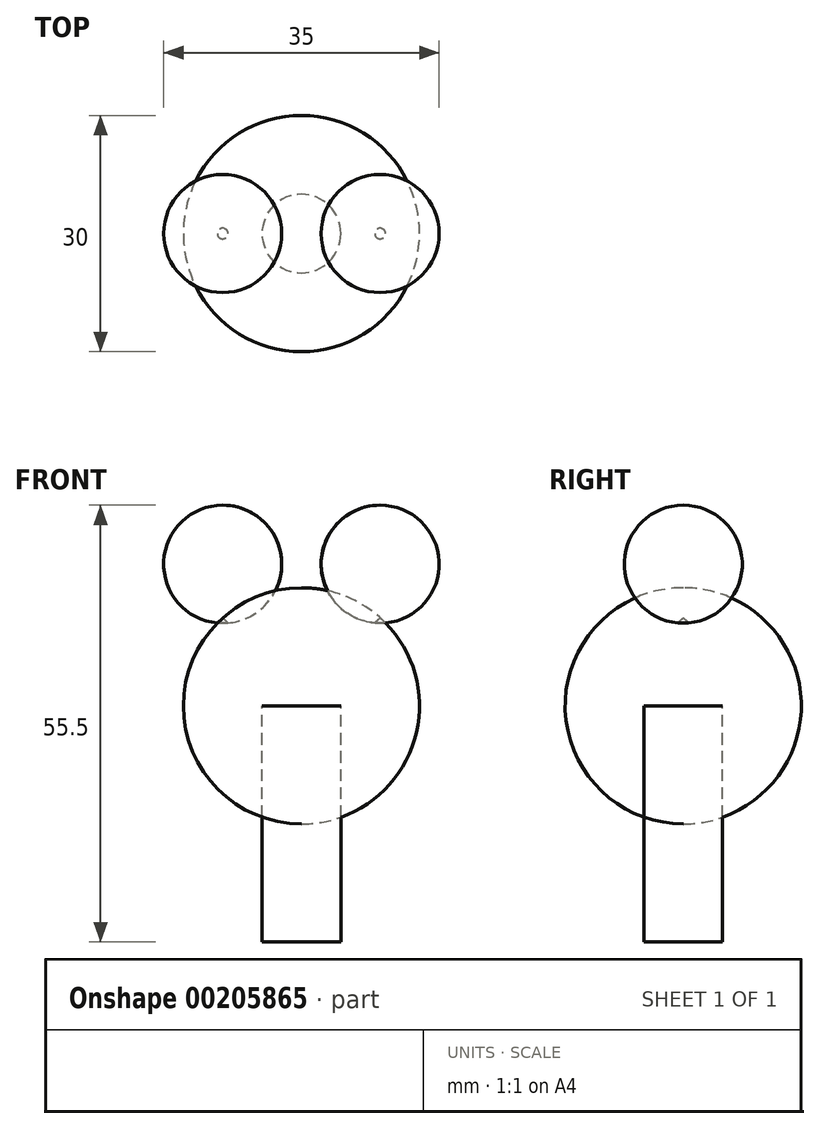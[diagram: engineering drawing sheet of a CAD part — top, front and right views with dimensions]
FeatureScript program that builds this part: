
annotation { "Feature Type Name" : "Feature", "Feature Type Description" : "" }
export const myFeature = defineFeature(function(context is Context, id is Id, definition is map)
    precondition{}
    {
        {
            var Q0;
            Q0=qCreatedBy(makeId("Front.planeOp"),FACE);
            var sketch = newSketch(context, id + "F0", { "sketchPlane" : qUnion([Q0])});
            skArc(sketch, "E0", {"start": v(0, 15) * mm, "mid": v(-15, 0) * mm, "end": v(0, -15) * mm});
            skArc(sketch, "E1", {"start": v(-10, 25.5) * mm, "mid": v(-17.5, 18) * mm, "end": v(-10, 10.5) * mm});
            skLineSegment(sketch, "E2", {"start": v(0, 49.4) * mm, "end": v(0, -36.14) * mm, "construction": true});
            skLineSegment(sketch, "E3", {"start": v(-10, 18) * mm, "end": v(-10, 43.94) * mm, "construction": true});
            skLineSegment(sketch, "E4", {"start": v(0, 15) * mm, "end": v(0, -15) * mm});
            skLineSegment(sketch, "E5", {"start": v(-10, 25.5) * mm, "end": v(-10, 10.5) * mm});
            skSolve(sketch);
        }
        {
            var Q0;
            {var subQ0=sQuery(id+"F0.wireOp",EDGE,"E4");Q0=makeQuery(id+"F0.imprint","IMPRINT",FACE,{"disambiguationData":[TD([[makeQuery(id+"F0.imprint","IMPRINT",EDGE,{"derivedFrom":subQ0}),-1.0]])]});}
            var Q1;
            {var subQ0=sQuery(id+"F0.wireOp",EDGE,"E5");var subQ1=sQuery(id+"F0.wireOp",EDGE,"E0");var subQ2=makeQuery(id+"F0.imprint","INTERSECT",VERTEX,{"derivedFrom":[subQ1,subQ0]});Q1=makeQuery(id+"F0.imprint","IMPRINT",FACE,{"disambiguationData":[TD([[makeQuery(id+"F0.imprint","IMPRINT",EDGE,{"disambiguationData":[TD([[subQ2,-1.0]])],"derivedFrom":subQ1}),1.0]])]});}
            var Q2;
            Q2=sQuery(id+"F0.wireOp",EDGE,"E2");
            revolve(context, id + "F1", {"entities" : qUnion([Q0, Q1]), "axis" : qUnion([Q2]), "revolveType" : RevolveType.FULL});
        }
        {
            var Q0;
            {var subQ0=sQuery(id+"F0.wireOp",EDGE,"E5");var subQ1=sQuery(id+"F0.wireOp",EDGE,"E0");var subQ2=makeQuery(id+"F0.imprint","INTERSECT",VERTEX,{"derivedFrom":[subQ1,subQ0]});Q0=makeQuery(id+"F0.imprint","IMPRINT",FACE,{"disambiguationData":[TD([[makeQuery(id+"F0.imprint","IMPRINT",EDGE,{"disambiguationData":[TD([[subQ2,-1.0]])],"derivedFrom":subQ1}),-1.0]])]});}
            var Q1;
            Q1=sQuery(id+"F0.wireOp",EDGE,"E5");
            revolve(context, id + "F2", {"entities" : qUnion([Q0]), "axis" : qUnion([Q1]), "revolveType" : RevolveType.FULL});
        }
        {
            var Q0;
            Q0=makeQuery(id+"F2.opRevolve","SWEPT_BODY",BODY,{"disambiguationData":[OSD([sQuery(id+"F0.wireOp",EDGE,"E0"),sQuery(id+"F0.wireOp",EDGE,"E1"),sQuery(id+"F0.wireOp",EDGE,"E5")])]});
            var Q1;
            Q1=qCreatedBy(makeId("Right.planeOp"),FACE);
            mirror(context, id + "F3", {"entities" : qUnion([Q0]), "mirrorPlane" : qUnion([Q1])});
        }
        {
            var Q0;
            Q0=qCreatedBy(makeId("Top.planeOp"),FACE);
            var sketch = newSketch(context, id + "F4", { "sketchPlane" : qUnion([Q0])});
            skCircle(sketch, "E6", {"center": v(0, 0) * mm, "radius": 5 * mm});
            skSolve(sketch);
        }
        {
            var Q0;
            Q0 = qSketchRegion(id + "F4", true);
            extrude(context, id + "F5", {"entities" : qUnion([Q0]), "oppositeDirection" : true, "depth" : 30 * mm});
        }
    });
